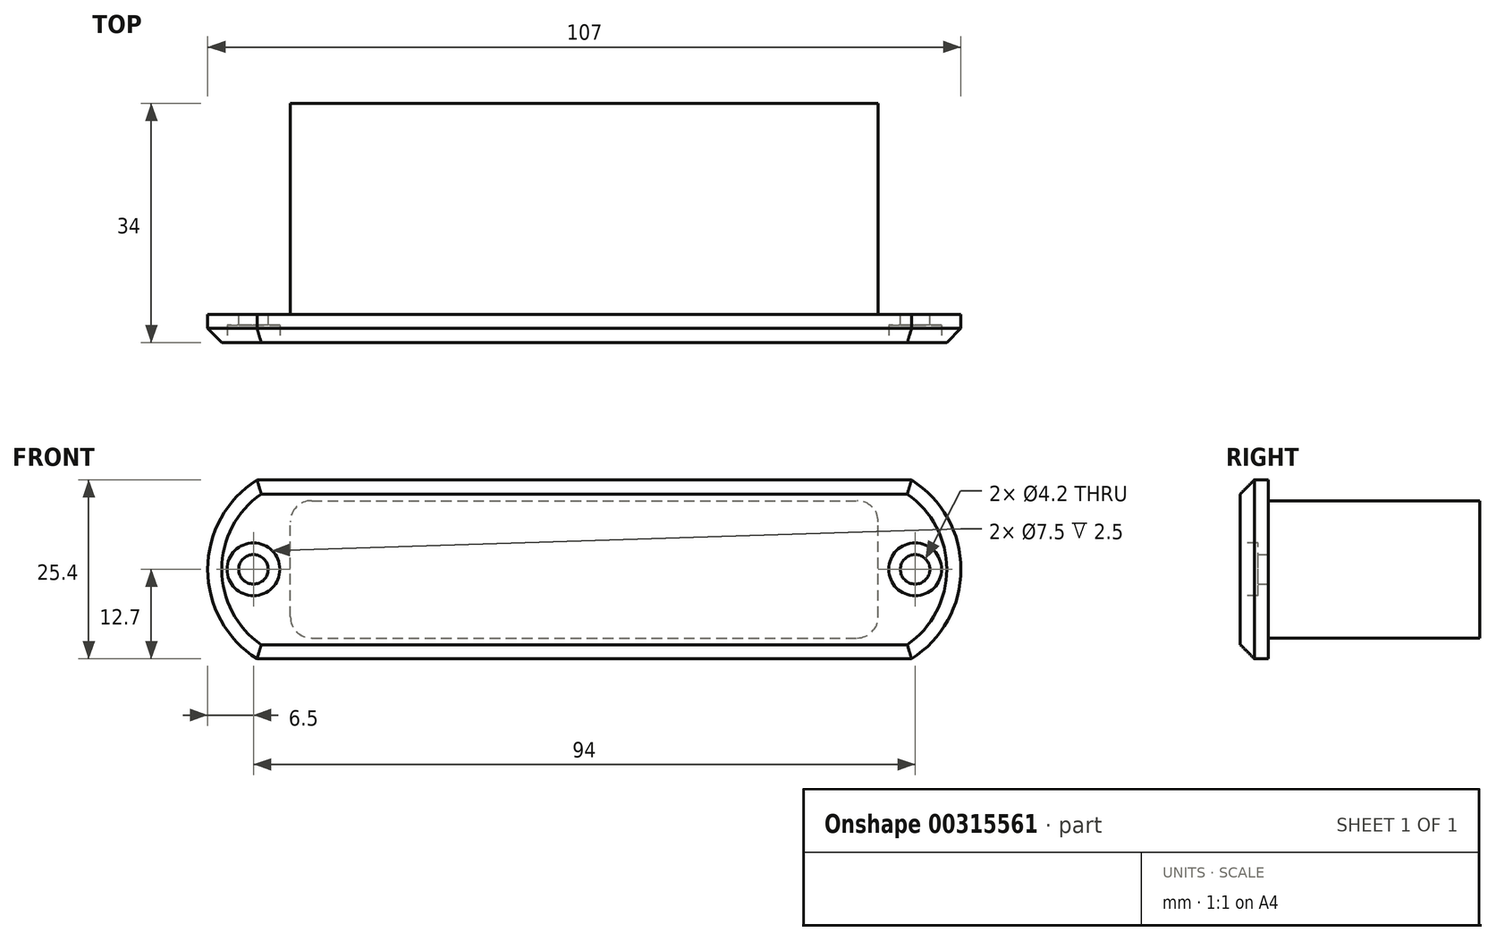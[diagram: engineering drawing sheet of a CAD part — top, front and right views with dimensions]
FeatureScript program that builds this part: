
annotation { "Feature Type Name" : "Feature", "Feature Type Description" : "" }
export const myFeature = defineFeature(function(context is Context, id is Id, definition is map)
    precondition{}
    {
        {
            var Q0;
            Q0=qCreatedBy(makeId("Front.planeOp"),FACE);
            var sketch = newSketch(context, id + "F0", { "sketchPlane" : qUnion([Q0])});
            skLineSegment(sketch, "E0", {"start": v(-46.48, 12.7) * mm, "end": v(0, 12.7) * mm});
            skLineSegment(sketch, "E1", {"start": v(0, 0) * mm, "end": v(0, 32.84) * mm, "construction": true});
            skLineSegment(sketch, "E2", {"start": v(-46.48, -12.7) * mm, "end": v(0, -12.7) * mm});
            skArc(sketch, "E3", {"start": v(-46.48, 12.7) * mm, "mid": v(-53.5, 0) * mm, "end": v(-46.48, -12.7) * mm});
            skLineSegment(sketch, "E4", {"start": v(0, 0) * mm, "end": v(-53.5, 0) * mm, "construction": true});
            skCircle(sketch, "E5", {"center": v(-47, 0) * mm, "radius": 2.1 * mm});
            skCircle(sketch, "E6.MirrorC", {"center": v(47, 0) * mm, "radius": 2.1 * mm});
            skLineSegment(sketch, "E7.MirrorCS", {"start": v(46.48, 12.7) * mm, "end": v(0, 12.7) * mm});
            skArc(sketch, "E8.MirrorCS", {"start": v(46.48, 12.7) * mm, "mid": v(53.5, 0) * mm, "end": v(46.48, -12.7) * mm});
            skLineSegment(sketch, "E9.MirrorCS", {"start": v(46.48, -12.7) * mm, "end": v(0, -12.7) * mm});
            skSolve(sketch);
        }
        {
            var Q0;
            Q0 = qSketchRegion(id + "F0", true);
            extrude(context, id + "F1", {"entities" : qUnion([Q0]), "depth" : 4 * mm});
        }
        {
            var Q0;
            Q0=makeQuery(id+"F1.opExtrude","CAP_EDGE",EDGE,{"disambiguationData":[OSD([sQuery(id+"F0.wireOp",EDGE,"E0"),sQuery(id+"F0.wireOp",EDGE,"E7.MirrorCS")])],"isStart":false});
            var Q1;
            Q1=makeQuery(id+"F1.opExtrude","CAP_EDGE",EDGE,{"disambiguationData":[OSD([sQuery(id+"F0.wireOp",EDGE,"E8.MirrorCS")])],"isStart":false});
            var Q2;
            Q2=makeQuery(id+"F1.opExtrude","CAP_EDGE",EDGE,{"disambiguationData":[OSD([sQuery(id+"F0.wireOp",EDGE,"E2"),sQuery(id+"F0.wireOp",EDGE,"E9.MirrorCS")])],"isStart":false});
            var Q3;
            Q3=makeQuery(id+"F1.opExtrude","CAP_EDGE",EDGE,{"disambiguationData":[OSD([sQuery(id+"F0.wireOp",EDGE,"E3")])],"isStart":false});
            chamfer(context, id + "F2", {"entities" : qUnion([Q0, Q1, Q2, Q3]), "width" : 2 * mm, "tangentPropagation" : true});
        }
        {
            var Q0;
            Q0=makeQuery(id+"F1.opExtrude","CAP_FACE",FACE,{"disambiguationData":[OSD([sQuery(id+"F0.wireOp",EDGE,"E0"),sQuery(id+"F0.wireOp",EDGE,"E2"),sQuery(id+"F0.wireOp",EDGE,"E3"),sQuery(id+"F0.wireOp",EDGE,"E5"),sQuery(id+"F0.wireOp",EDGE,"E6.MirrorC"),sQuery(id+"F0.wireOp",EDGE,"E7.MirrorCS"),sQuery(id+"F0.wireOp",EDGE,"E8.MirrorCS"),sQuery(id+"F0.wireOp",EDGE,"E9.MirrorCS")])],"isStart":false});
            var sketch = newSketch(context, id + "F3", { "sketchPlane" : qUnion([Q0])});
            skCircle(sketch, "E10", {"center": v(-47, 0) * mm, "radius": 3.75 * mm});
            skCircle(sketch, "E11", {"center": v(47, 0) * mm, "radius": 3.75 * mm});
            skSolve(sketch);
        }
        {
            var Q0;
            Q0 = qSketchRegion(id + "F3", true);
            extrude(context, id + "F4", {"entities" : qUnion([Q0]), "operationType" : NewBodyOperationType.REMOVE, "oppositeDirection" : true, "depth" : 2.5 * mm});
        }
        {
            var Q0;
            Q0=makeQuery(id+"F1.opExtrude","CAP_FACE",FACE,{"disambiguationData":[OSD([sQuery(id+"F0.wireOp",EDGE,"E0"),sQuery(id+"F0.wireOp",EDGE,"E2"),sQuery(id+"F0.wireOp",EDGE,"E3"),sQuery(id+"F0.wireOp",EDGE,"E5"),sQuery(id+"F0.wireOp",EDGE,"E6.MirrorC"),sQuery(id+"F0.wireOp",EDGE,"E7.MirrorCS"),sQuery(id+"F0.wireOp",EDGE,"E8.MirrorCS"),sQuery(id+"F0.wireOp",EDGE,"E9.MirrorCS")])],"isStart":true});
            var sketch = newSketch(context, id + "F5", { "sketchPlane" : qUnion([Q0])});
            skLineSegment(sketch, "E12.bottom", {"start": v(41.75, -9.75) * mm, "end": v(-41.75, -9.75) * mm});
            skLineSegment(sketch, "E12.top", {"start": v(41.75, 9.75) * mm, "end": v(-41.75, 9.75) * mm});
            skLineSegment(sketch, "E12.left", {"start": v(41.75, -9.75) * mm, "end": v(41.75, 9.75) * mm});
            skLineSegment(sketch, "E12.right", {"start": v(-41.75, -9.75) * mm, "end": v(-41.75, 9.75) * mm});
            skPoint(sketch, "E12.middle", {"position": v(0, 0) * mm});
            skSolve(sketch);
        }
        {
            var Q0;
            Q0 = qSketchRegion(id + "F5", true);
            extrude(context, id + "F6", {"entities" : qUnion([Q0]), "operationType" : NewBodyOperationType.ADD, "depth" : 30 * mm});
        }
        {
            var Q0;
            Q0=makeQuery(id+"F6.opExtrude","SWEPT_EDGE",EDGE,{"disambiguationData":[OSD([sQuery(id+"F5.wireOp",EDGE,"E12.top"),sQuery(id+"F5.wireOp",EDGE,"E12.right")])]});
            var Q1;
            Q1=makeQuery(id+"F6.opExtrude","SWEPT_EDGE",EDGE,{"disambiguationData":[OSD([sQuery(id+"F5.wireOp",EDGE,"E12.top"),sQuery(id+"F5.wireOp",EDGE,"E12.left")])]});
            var Q2;
            Q2=makeQuery(id+"F6.opExtrude","SWEPT_EDGE",EDGE,{"disambiguationData":[OSD([sQuery(id+"F5.wireOp",EDGE,"E12.bottom"),sQuery(id+"F5.wireOp",EDGE,"E12.left")])]});
            var Q3;
            Q3=makeQuery(id+"F6.opExtrude","SWEPT_EDGE",EDGE,{"disambiguationData":[OSD([sQuery(id+"F5.wireOp",EDGE,"E12.bottom"),sQuery(id+"F5.wireOp",EDGE,"E12.right")])]});
            fillet(context, id + "F7", {"entities" : qUnion([Q0, Q1, Q2, Q3]), "radius" : 3 * mm, "tangentPropagation" : true, "allowEdgeOverflow" : false});
        }
    });
